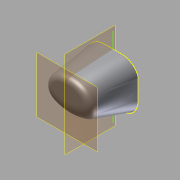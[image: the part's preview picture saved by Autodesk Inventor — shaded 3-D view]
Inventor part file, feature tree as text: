
AUTODESK INVENTOR PART (.ipt)
format: ipt  version: 2012 (Build 160160000, 160)  size: 448,000 bytes
history: native  units: in
note: dims shown in document units (in); Inventor stores cm internally (conversion verified against a paired STEP export)
features: sketch x8, fillet x4, plane x3, extrude x3, loft x1, revolve x1
ambient origin geometry x8: Origin, YZ Plane, XZ Plane, XY Plane, X Axis, Y Axis, Z Axis, Center Point
bodies: Solid1 (feature_tree)
feature tree (20):
  sketch  "Sketch1"  dims[d0=3.45in d1=3.8075in]
  plane  "Work Plane2"
  loft  "Loft1"
  sketch  "Sketch5"  dims[d4=3.4895in d6=2.53in]
  plane  "Work Plane4"
  revolve  "Revolution1"  [1 undecoded]
  extrude  "Extrusion1"  Depth=2.53in
  sketch  "Sketch9"  dims[d34=2.4755in]
  extrude  "Extrusion2"  TaperAngle=0.0deg  [1 undecoded]
  extrude  "Extrusion3"  TaperAngle=180.0deg  [1 undecoded]
  fillet  "Fillet6"  Radius=5.0in
  fillet  "Fillet8"  Radius=1.047in
  fillet  "Fillet9"  Radius=0.5235in
  fillet  "Fillet11"  Radius=1.047in
  plane  "Work Plane1"
  sketch  "Sketch2"  dims[d2=1.4385in d3=2.766in]
  sketch  "Sketch6"  dims[d8=0.0in d10=0.0in d11=90.0deg]
  sketch  "Sketch7"  dims[d12=0.0in d13=90.0deg d19=180.0deg d20=5.0in d21=0.0in d31=1.047in d32=0.5235in d33=1.047in]
  sketch  "Sketch10"  dims[d42=0.4745in]
  sketch  "Sketch11"  dims[d43=1.047in d44=0.0in d45=2.4755in d46=0.0in d49=0.5445in d50=2.4755in d51=0.0in d52=0.125in d54=1.4385in d55=1.4385in d58=1.6885in d59=0.8443in d60=1.9811in d61=0.25in d62=90.0deg d63=0.5235in d64=0.125in d65=0.8in d66=0.8in d67=0.4in d68=0.2047in d73=0.0in d74=0.0in d75=1.0in d76=0.1969in d77=1.7in]
note: 3 required parameter values undecoded (feature->parameter linkage not recoverable at this tier; creation-order binding heuristic only, values carry confidence <= 0.55)